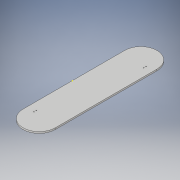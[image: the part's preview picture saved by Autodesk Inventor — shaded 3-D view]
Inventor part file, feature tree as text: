
AUTODESK INVENTOR PART (.ipt)
format: ipt  version: 2019 (Build 230136000, 136)  size: 135,680 bytes
history: native  units: mm
features: sketch x4, hole x2, other x1, extrude x1
ambient origin geometry x8: Origin, YZ Plane, XZ Plane, XY Plane, X Axis, Y Axis, Z Axis, Center Point
bodies: Body1 (feature_tree)
feature tree (8):
  other  "ソリッド1"
  sketch  "スケッチ1"
  extrude  "押し出し1"  Depth=270.0mm
  hole  "穴4"  [1 undecoded]
  hole  "穴5"  [1 undecoded]
  sketch  "スケッチ2"
  sketch  "スケッチ6"
  sketch  "スケッチ7"
note: 2 required parameter values undecoded (feature->parameter linkage not recoverable at this tier; creation-order binding heuristic only, values carry confidence <= 0.55)
